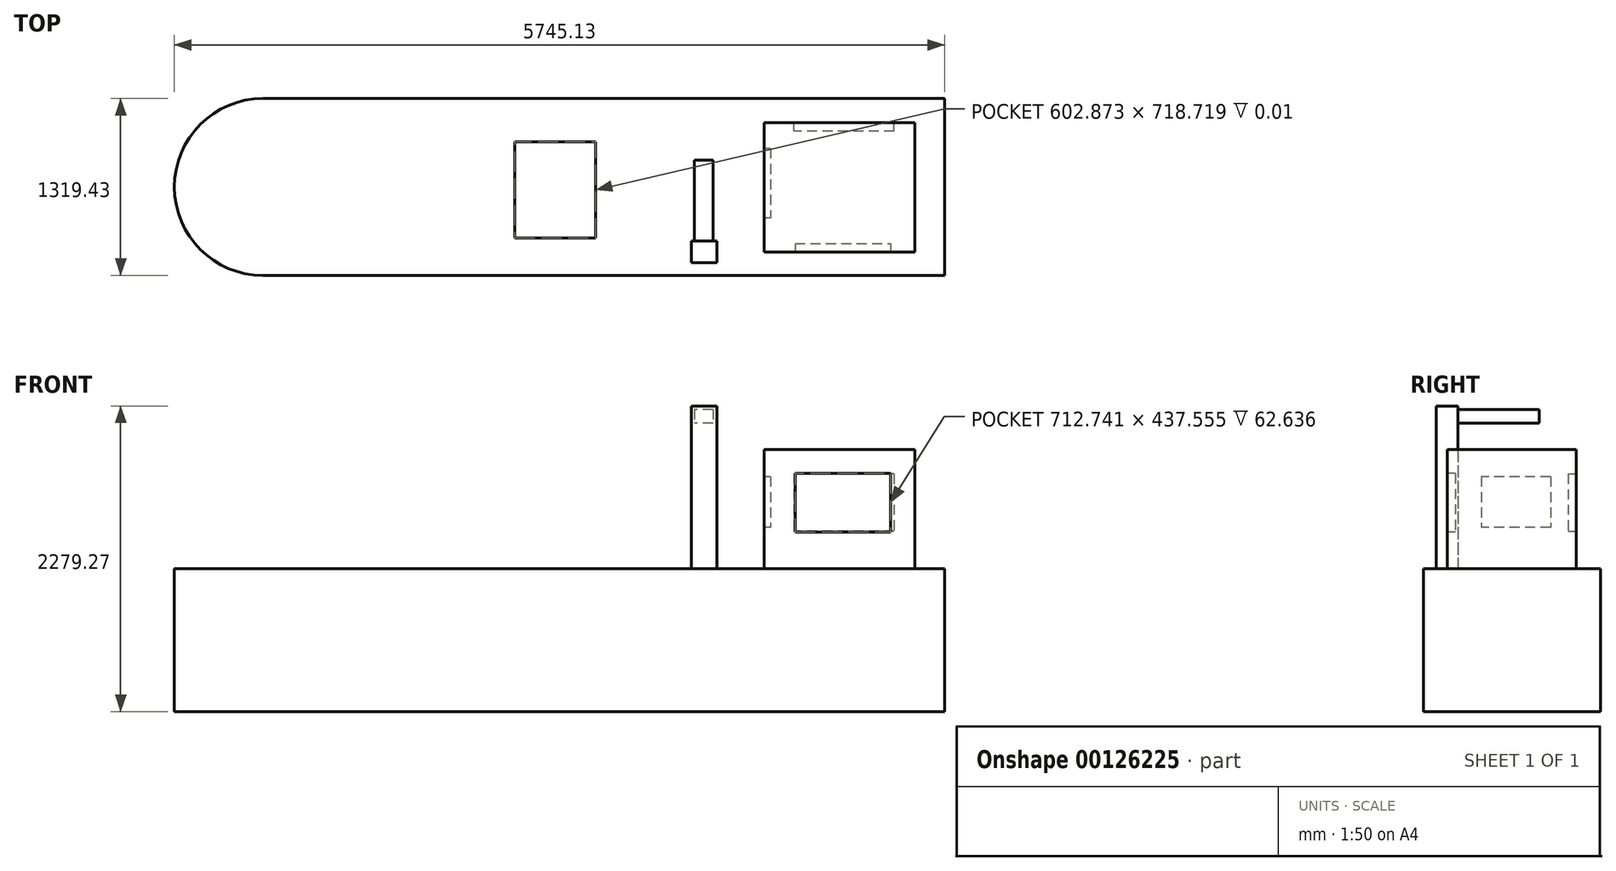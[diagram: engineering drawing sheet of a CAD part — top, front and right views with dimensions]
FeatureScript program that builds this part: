
annotation { "Feature Type Name" : "Feature", "Feature Type Description" : "" }
export const myFeature = defineFeature(function(context is Context, id is Id, definition is map)
    precondition{}
    {
        {
            var Q0;
            Q0=qCreatedBy(makeId("Top.planeOp"),FACE);
            var sketch = newSketch(context, id + "F0", { "sketchPlane" : qUnion([Q0])});
            skLineSegment(sketch, "E0", {"start": v(0, 60.95) * mm, "end": v(1275.36, 60.95) * mm});
            skLineSegment(sketch, "E1", {"start": v(1275.36, 60.95) * mm, "end": v(5085.41, 60.95) * mm});
            skLineSegment(sketch, "E2", {"start": v(5085.41, 60.95) * mm, "end": v(5085.41, -1258.48) * mm});
            skLineSegment(sketch, "E3", {"start": v(5085.41, -1258.48) * mm, "end": v(0, -1258.48) * mm});
            skArc(sketch, "E4", {"start": v(0, 60.95) * mm, "mid": v(-659.72, -598.76) * mm, "end": v(0, -1258.48) * mm});
            skSolve(sketch);
        }
        {
            var Q0;
            Q0=makeQuery(id+"F0.imprint","IMPRINT",FACE,{"disambiguationData":[TD([[makeQuery(id+"F0.imprint","IMPRINT",EDGE,{"derivedFrom":sQuery(id+"F0.wireOp",EDGE,"E0")}),-1.0]])]});
            extrude(context, id + "F1", {"entities" : qUnion([Q0]), "depth" : 1041.7 * mm});
        }
        {
            var Q0;
            Q0=makeQuery(id+"F1.opExtrude","CAP_FACE",FACE,{"disambiguationData":[OSD([sQuery(id+"F0.wireOp",EDGE,"E0"),sQuery(id+"F0.wireOp",EDGE,"E1"),sQuery(id+"F0.wireOp",EDGE,"E2"),sQuery(id+"F0.wireOp",EDGE,"E3"),sQuery(id+"F0.wireOp",EDGE,"E4")])],"isStart":false});
            var sketch = newSketch(context, id + "F2", { "sketchPlane" : qUnion([Q0])});
            skLineSegment(sketch, "E5.bottom", {"start": v(4864.85, -119.32) * mm, "end": v(3738.79, -119.32) * mm});
            skLineSegment(sketch, "E5.top", {"start": v(4864.85, -1083.2) * mm, "end": v(3738.79, -1083.2) * mm});
            skLineSegment(sketch, "E5.left", {"start": v(4864.85, -119.32) * mm, "end": v(4864.85, -1083.2) * mm});
            skLineSegment(sketch, "E5.right", {"start": v(3738.79, -119.32) * mm, "end": v(3738.79, -1083.2) * mm});
            skSolve(sketch);
        }
        {
            var Q0;
            Q0 = qSketchRegion(id + "F2", true);
            extrude(context, id + "F3", {"entities" : qUnion([Q0]), "operationType" : NewBodyOperationType.ADD, "depth" : 912.2 * mm});
        }
        {
            var Q0;
            Q0=makeQuery(id+"F1.opExtrude","CAP_FACE",FACE,{"disambiguationData":[OSD([sQuery(id+"F0.wireOp",EDGE,"E0"),sQuery(id+"F0.wireOp",EDGE,"E1"),sQuery(id+"F0.wireOp",EDGE,"E2"),sQuery(id+"F0.wireOp",EDGE,"E3"),sQuery(id+"F0.wireOp",EDGE,"E4")])],"isStart":false});
            var sketch = newSketch(context, id + "F4", { "sketchPlane" : qUnion([Q0])});
            skSolve(sketch);
        }
        {
            var Q0;
            Q0=makeQuery(id+"F4.imprint","IMPRINT",FACE,{"disambiguationData":[TD([[makeQuery(id+"F4.imprint","IMPRINT",EDGE,{"derivedFrom":makeQuery(id+"F1.opExtrude","CAP_EDGE",EDGE,{"disambiguationData":[OSD([sQuery(id+"F0.wireOp",EDGE,"E2")])],"isStart":false})}),-1.0]])]});
            extrude(context, id + "F5", {"entities" : qUnion([Q0]), "operationType" : NewBodyOperationType.ADD, "depth" : 25.4 * mm});
        }
        {
            var Q0;
            Q0=makeQuery(id+"F5.opExtrude","CAP_FACE",FACE,{"disambiguationData":[OSD([sQuery(id+"F0.wireOp",EDGE,"E0"),sQuery(id+"F0.wireOp",EDGE,"E1"),sQuery(id+"F0.wireOp",EDGE,"E2"),sQuery(id+"F0.wireOp",EDGE,"E3"),sQuery(id+"F0.wireOp",EDGE,"E4"),sQuery(id+"F2.wireOp",EDGE,"E5.bottom"),sQuery(id+"F2.wireOp",EDGE,"E5.top"),sQuery(id+"F2.wireOp",EDGE,"E5.left"),sQuery(id+"F2.wireOp",EDGE,"E5.right")])],"isStart":false});
            var sketch = newSketch(context, id + "F6", { "sketchPlane" : qUnion([Q0])});
            skSolve(sketch);
        }
        {
            var Q0;
            Q0=makeQuery(id+"F3.opExtrude","SWEPT_FACE",FACE,{"disambiguationData":[OSD([sQuery(id+"F2.wireOp",EDGE,"E5.right")])]});
            var sketch = newSketch(context, id + "F7", { "sketchPlane" : qUnion([Q0])});
            skLineSegment(sketch, "E6.bottom", {"start": v(312.1, 1752.94) * mm, "end": v(828.86, 1752.94) * mm});
            skLineSegment(sketch, "E6.top", {"start": v(312.1, 1372.72) * mm, "end": v(828.86, 1372.72) * mm});
            skLineSegment(sketch, "E6.left", {"start": v(312.1, 1752.94) * mm, "end": v(312.1, 1372.72) * mm});
            skLineSegment(sketch, "E6.right", {"start": v(828.86, 1752.94) * mm, "end": v(828.86, 1372.72) * mm});
            skSolve(sketch);
        }
        {
            var Q0;
            Q0 = qSketchRegion(id + "F7", true);
            extrude(context, id + "F8", {"entities" : qUnion([Q0]), "operationType" : NewBodyOperationType.REMOVE, "oppositeDirection" : true, "depth" : 1 / 812.8 * mm});
        }
        {
            var Q0;
            Q0 = qSketchRegion(id + "F7", true);
            extrude(context, id + "F9", {"entities" : qUnion([Q0]), "operationType" : NewBodyOperationType.REMOVE, "oppositeDirection" : true, "depth" : 49.57 * mm});
        }
        {
            var Q0;
            Q0=makeQuery(id+"F3.opExtrude","SWEPT_FACE",FACE,{"disambiguationData":[OSD([sQuery(id+"F2.wireOp",EDGE,"E5.bottom")])]});
            var sketch = newSketch(context, id + "F10", { "sketchPlane" : qUnion([Q0])});
            skLineSegment(sketch, "E7.bottom", {"start": v(-4709.4, 1773.2) * mm, "end": v(-3960.49, 1773.2) * mm});
            skLineSegment(sketch, "E7.top", {"start": v(-4709.4, 1345.48) * mm, "end": v(-3960.49, 1345.48) * mm});
            skLineSegment(sketch, "E7.left", {"start": v(-4709.4, 1773.2) * mm, "end": v(-4709.4, 1345.48) * mm});
            skLineSegment(sketch, "E7.right", {"start": v(-3960.49, 1773.2) * mm, "end": v(-3960.49, 1345.48) * mm});
            skSolve(sketch);
        }
        {
            var Q0;
            Q0 = qSketchRegion(id + "F10", true);
            var Q1;
            Q1=makeQuery(id+"F10.imprint","IMPRINT",FACE,{"disambiguationData":[TD([[makeQuery(id+"F10.imprint","IMPRINT",EDGE,{"derivedFrom":sQuery(id+"F10.wireOp",EDGE,"E7.bottom")}),-1.0]])]});
            extrude(context, id + "F11", {"entities" : qUnion([Q0, Q1]), "operationType" : NewBodyOperationType.REMOVE, "oppositeDirection" : true, "depth" : 62.64 * mm});
        }
        {
            var Q0;
            Q0=makeQuery(id+"F3.opExtrude","SWEPT_FACE",FACE,{"disambiguationData":[OSD([sQuery(id+"F2.wireOp",EDGE,"E5.top")])]});
            var sketch = newSketch(context, id + "F12", { "sketchPlane" : qUnion([Q0])});
            skLineSegment(sketch, "E8.bottom", {"start": v(3970.25, 1776.13) * mm, "end": v(4682.99, 1776.13) * mm});
            skLineSegment(sketch, "E8.top", {"start": v(3970.25, 1338.57) * mm, "end": v(4682.99, 1338.57) * mm});
            skLineSegment(sketch, "E8.left", {"start": v(3970.25, 1776.13) * mm, "end": v(3970.25, 1338.57) * mm});
            skLineSegment(sketch, "E8.right", {"start": v(4682.99, 1776.13) * mm, "end": v(4682.99, 1338.57) * mm});
            skSolve(sketch);
        }
        {
            var Q0;
            Q0 = qSketchRegion(id + "F12", true);
            extrude(context, id + "F13", {"entities" : qUnion([Q0]), "operationType" : NewBodyOperationType.REMOVE, "oppositeDirection" : true, "depth" : 62.64 * mm});
        }
        {
            var Q0;
            Q0=makeQuery(id+"F6.imprint","IMPRINT",FACE,{"disambiguationData":[TD([[makeQuery(id+"F6.imprint","IMPRINT",EDGE,{"derivedFrom":makeQuery(id+"F5.opExtrude","CAP_EDGE",EDGE,{"disambiguationData":[OSD([sQuery(id+"F0.wireOp",EDGE,"E2")])],"isStart":false})}),-1.0]])]});
            var sketch = newSketch(context, id + "F14", { "sketchPlane" : qUnion([Q0])});
            skLineSegment(sketch, "E9.bottom", {"start": v(2481.62, -260.99) * mm, "end": v(1878.75, -260.99) * mm});
            skLineSegment(sketch, "E9.top", {"start": v(2481.62, -979.7) * mm, "end": v(1878.75, -979.7) * mm});
            skLineSegment(sketch, "E9.left", {"start": v(2481.62, -260.99) * mm, "end": v(2481.62, -979.7) * mm});
            skLineSegment(sketch, "E9.right", {"start": v(1878.75, -260.99) * mm, "end": v(1878.75, -979.7) * mm});
            skSolve(sketch);
        }
        {
            var Q0;
            Q0 = qSketchRegion(id + "F14", true);
            extrude(context, id + "F15", {"entities" : qUnion([Q0]), "operationType" : NewBodyOperationType.REMOVE, "oppositeDirection" : true, "depth" : 1 / 101.6 * mm});
        }
        {
            var Q0;
            Q0=makeQuery(id+"F6.imprint","IMPRINT",FACE,{"disambiguationData":[TD([[makeQuery(id+"F6.imprint","IMPRINT",EDGE,{"derivedFrom":makeQuery(id+"F5.opExtrude","CAP_EDGE",EDGE,{"disambiguationData":[OSD([sQuery(id+"F0.wireOp",EDGE,"E2")])],"isStart":false})}),-1.0]])]});
            var sketch = newSketch(context, id + "F16", { "sketchPlane" : qUnion([Q0])});
            skLineSegment(sketch, "E10.bottom", {"start": v(3196.36, -1003.1) * mm, "end": v(3386.54, -1003.1) * mm});
            skLineSegment(sketch, "E10.top", {"start": v(3196.36, -1164.55) * mm, "end": v(3386.54, -1164.55) * mm});
            skLineSegment(sketch, "E10.left", {"start": v(3196.36, -1003.1) * mm, "end": v(3196.36, -1164.55) * mm});
            skLineSegment(sketch, "E10.right", {"start": v(3386.54, -1003.1) * mm, "end": v(3386.54, -1164.55) * mm});
            skSolve(sketch);
        }
        {
            var Q0;
            Q0 = qSketchRegion(id + "F16", true);
            extrude(context, id + "F17", {"entities" : qUnion([Q0]), "operationType" : NewBodyOperationType.ADD, "depth" : 1212.18 * mm});
        }
        {
            var Q0;
            Q0=makeQuery(id+"F17.opExtrude","SWEPT_FACE",FACE,{"disambiguationData":[OSD([sQuery(id+"F16.wireOp",EDGE,"E10.bottom")])]});
            var sketch = newSketch(context, id + "F18", { "sketchPlane" : qUnion([Q0])});
            skLineSegment(sketch, "E11.bottom", {"start": v(-3357.42, 2254) * mm, "end": v(-3219.95, 2254) * mm});
            skLineSegment(sketch, "E11.top", {"start": v(-3357.42, 2153) * mm, "end": v(-3219.95, 2153) * mm});
            skLineSegment(sketch, "E11.left", {"start": v(-3357.42, 2254) * mm, "end": v(-3357.42, 2153) * mm});
            skLineSegment(sketch, "E11.right", {"start": v(-3219.95, 2254) * mm, "end": v(-3219.95, 2153) * mm});
            skSolve(sketch);
        }
        {
            var Q0;
            Q0 = qSketchRegion(id + "F18", true);
            extrude(context, id + "F19", {"entities" : qUnion([Q0]), "operationType" : NewBodyOperationType.ADD, "depth" : 605.9 * mm});
        }
    });
